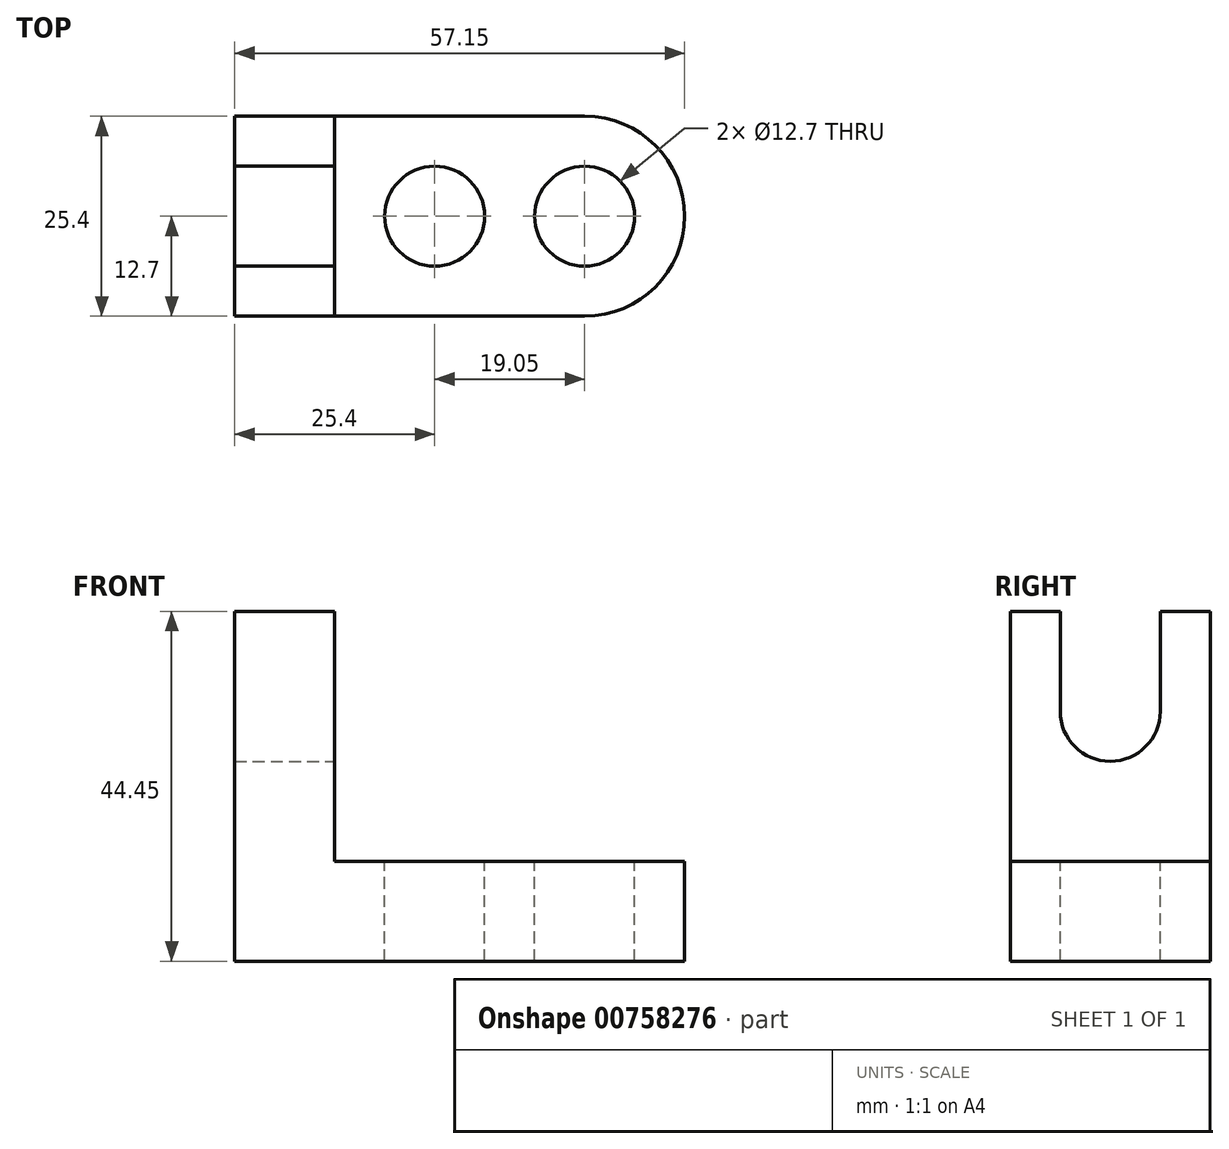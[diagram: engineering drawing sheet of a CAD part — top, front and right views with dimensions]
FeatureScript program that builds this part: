
annotation { "Feature Type Name" : "Feature", "Feature Type Description" : "" }
export const myFeature = defineFeature(function(context is Context, id is Id, definition is map)
    precondition{}
    {
        {
            var Q0;
            Q0=qCreatedBy(makeId("Front.planeOp"),FACE);
            var sketch = newSketch(context, id + "F0", { "sketchPlane" : qUnion([Q0])});
            skLineSegment(sketch, "E0", {"start": v(0, 0) * mm, "end": v(57.15, 0) * mm});
            skLineSegment(sketch, "E1", {"start": v(57.15, 0) * mm, "end": v(57.15, 44.45) * mm});
            skLineSegment(sketch, "E2", {"start": v(57.15, 44.45) * mm, "end": v(0, 44.45) * mm});
            skLineSegment(sketch, "E3", {"start": v(0, 44.45) * mm, "end": v(0, 0) * mm});
            skSolve(sketch);
        }
        {
            var Q0;
            Q0=makeQuery(id+"F0.imprint","IMPRINT",FACE,{"disambiguationData":[TD([[makeQuery(id+"F0.imprint","IMPRINT",EDGE,{"derivedFrom":sQuery(id+"F0.wireOp",EDGE,"E0")}),1.0]])]});
            extrude(context, id + "F1", {"entities" : qUnion([Q0]), "depth" : 25.4 * mm, "offsetDistance" : 25.4 * mm});
        }
        {
            var Q0;
            Q0=makeQuery(id+"F1.opExtrude","CAP_FACE",FACE,{"disambiguationData":[OSD([sQuery(id+"F0.wireOp",EDGE,"E0"),sQuery(id+"F0.wireOp",EDGE,"E1"),sQuery(id+"F0.wireOp",EDGE,"E2"),sQuery(id+"F0.wireOp",EDGE,"E3")])],"isStart":false});
            var sketch = newSketch(context, id + "F2", { "sketchPlane" : qUnion([Q0])});
            skLineSegment(sketch, "E4", {"start": v(12.7, 44.45) * mm, "end": v(12.7, 12.7) * mm});
            skLineSegment(sketch, "E5", {"start": v(12.7, 12.7) * mm, "end": v(57.15, 12.7) * mm});
            skSolve(sketch);
        }
        {
            var Q0;
            {var subQ0=sQuery(id+"F2.wireOp",EDGE,"E4");Q0=makeQuery(id+"F2.imprint","IMPRINT",FACE,{"disambiguationData":[TD([[makeQuery(id+"F2.imprint","IMPRINT",EDGE,{"derivedFrom":subQ0}),1.0]])]});}
            extrude(context, id + "F3", {"entities" : qUnion([Q0]), "operationType" : NewBodyOperationType.REMOVE, "oppositeDirection" : true, "depth" : 25.4 * mm, "offsetDistance" : 25.4 * mm});
        }
        {
            var Q0;
            Q0=makeQuery(id+"F3.boolean.opBoolean","COPY",FACE,{"derivedFrom":makeQuery(id+"F3.opExtrude","SWEPT_FACE",FACE,{"disambiguationData":[OSD([sQuery(id+"F2.wireOp",EDGE,"E5")])]})});
            var sketch = newSketch(context, id + "F4", { "sketchPlane" : qUnion([Q0])});
            skCircle(sketch, "E6", {"center": v(25.4, -12.7) * mm, "radius": 6.35 * mm});
            skCircle(sketch, "E7", {"center": v(44.45, -12.7) * mm, "radius": 6.35 * mm});
            skSolve(sketch);
        }
        {
            var Q0;
            Q0=makeQuery(id+"F4.imprint","IMPRINT",FACE,{"disambiguationData":[TD([[makeQuery(id+"F4.imprint","IMPRINT",EDGE,{"derivedFrom":sQuery(id+"F4.wireOp",EDGE,"E6")}),1.0]])]});
            var Q1;
            Q1=makeQuery(id+"F4.imprint","IMPRINT",FACE,{"disambiguationData":[TD([[makeQuery(id+"F4.imprint","IMPRINT",EDGE,{"derivedFrom":sQuery(id+"F4.wireOp",EDGE,"E7")}),1.0]])]});
            extrude(context, id + "F5", {"entities" : qUnion([Q0, Q1]), "operationType" : NewBodyOperationType.REMOVE, "oppositeDirection" : true, "depth" : 25.4 * mm, "offsetDistance" : 25.4 * mm});
        }
        {
            var Q0;
            Q0=makeQuery(id+"F3.boolean.opBoolean","COPY",FACE,{"derivedFrom":makeQuery(id+"F3.opExtrude","SWEPT_FACE",FACE,{"disambiguationData":[OSD([sQuery(id+"F2.wireOp",EDGE,"E5")])]})});
            var sketch = newSketch(context, id + "F6", { "sketchPlane" : qUnion([Q0])});
            skArc(sketch, "E8", {"start": v(44.45, -25.4) * mm, "mid": v(57.15, -12.7) * mm, "end": v(44.45, 0) * mm});
            skSolve(sketch);
        }
        {
            var Q0;
            {var subQ0=sQuery(id+"F6.wireOp",EDGE,"E8");var subQ1=sQuery(id+"F2.wireOp",EDGE,"E5");var subQ2=makeQuery(id+"F3.boolean.opBoolean","COPY",EDGE,{"derivedFrom":makeQuery(id+"F3.opExtrude","CAP_EDGE",EDGE,{"disambiguationData":[OSD([subQ1])],"isStart":false})});var subQ3=makeQuery(id+"F6.imprint","INTERSECT",VERTEX,{"derivedFrom":[subQ2,subQ0]});Q0=makeQuery(id+"F6.imprint","IMPRINT",FACE,{"disambiguationData":[TD([[makeQuery(id+"F6.imprint","IMPRINT",EDGE,{"disambiguationData":[TD([[subQ3,1.0]])],"derivedFrom":subQ0}),-1.0]])]});}
            var Q1;
            {var subQ0=sQuery(id+"F6.wireOp",EDGE,"E8");var subQ1=sQuery(id+"F2.wireOp",EDGE,"E5");var subQ2=makeQuery(id+"F3.boolean.opBoolean","COPY",EDGE,{"derivedFrom":makeQuery(id+"F3.opExtrude","CAP_EDGE",EDGE,{"disambiguationData":[OSD([subQ1])],"isStart":true})});var subQ3=makeQuery(id+"F6.imprint","INTERSECT",VERTEX,{"derivedFrom":[subQ2,subQ0]});Q1=makeQuery(id+"F6.imprint","IMPRINT",FACE,{"disambiguationData":[TD([[makeQuery(id+"F6.imprint","IMPRINT",EDGE,{"disambiguationData":[TD([[subQ3,-1.0]])],"derivedFrom":subQ0}),-1.0]])]});}
            extrude(context, id + "F7", {"entities" : qUnion([Q0, Q1]), "operationType" : NewBodyOperationType.REMOVE, "oppositeDirection" : true, "depth" : 25.4 * mm, "offsetDistance" : 25.4 * mm});
        }
        {
            var Q0;
            Q0=makeQuery(id+"F3.boolean.opBoolean","COPY",FACE,{"derivedFrom":makeQuery(id+"F3.opExtrude","SWEPT_FACE",FACE,{"disambiguationData":[OSD([sQuery(id+"F2.wireOp",EDGE,"E4")])]})});
            var sketch = newSketch(context, id + "F8", { "sketchPlane" : qUnion([Q0])});
            skCircle(sketch, "E9", {"center": v(-12.7, 31.75) * mm, "radius": 6.35 * mm});
            skLineSegment(sketch, "E10", {"start": v(-19.05, 31.75) * mm, "end": v(-19.05, 44.45) * mm});
            skLineSegment(sketch, "E11", {"start": v(-6.35, 31.75) * mm, "end": v(-6.35, 44.45) * mm});
            skArc(sketch, "E12", {"start": v(0, 31.75) * mm, "mid": v(-12.7, 44.45) * mm, "end": v(-25.4, 31.75) * mm});
            skPoint(sketch, "E12.endSnap0", {"position": v(-25.4, 28.57) * mm});
            skSolve(sketch);
        }
        {
            var Q0;
            {var subQ1=sQuery(id+"F2.wireOp",EDGE,"E4");var subQ4=sQuery(id+"F8.wireOp",EDGE,"E12");var subQ6=makeQuery(id+"F3.boolean.opBoolean","COPY",EDGE,{"derivedFrom":makeQuery(id+"F3.opExtrude","CAP_EDGE",EDGE,{"disambiguationData":[OSD([subQ1])],"isStart":true})});var subQ7=makeQuery(id+"F8.imprint","INTERSECT",VERTEX,{"derivedFrom":[subQ6,subQ4]});Q0=makeQuery(id+"F8.imprint","IMPRINT",FACE,{"disambiguationData":[TD([[makeQuery(id+"F8.imprint","IMPRINT",EDGE,{"disambiguationData":[TD([[subQ7,1.0]])],"derivedFrom":subQ4}),-1.0]])]});}
            var Q1;
            {var subQ1=sQuery(id+"F2.wireOp",EDGE,"E4");var subQ4=sQuery(id+"F8.wireOp",EDGE,"E12");var subQ6=makeQuery(id+"F3.boolean.opBoolean","COPY",EDGE,{"derivedFrom":makeQuery(id+"F3.opExtrude","CAP_EDGE",EDGE,{"disambiguationData":[OSD([subQ1])],"isStart":false})});var subQ7=makeQuery(id+"F8.imprint","INTERSECT",VERTEX,{"derivedFrom":[subQ6,subQ4]});Q1=makeQuery(id+"F8.imprint","IMPRINT",FACE,{"disambiguationData":[TD([[makeQuery(id+"F8.imprint","IMPRINT",EDGE,{"disambiguationData":[TD([[subQ7,-1.0]])],"derivedFrom":subQ4}),-1.0]])]});}
            var Q2;
            {var subQ0=sQuery(id+"F8.wireOp",EDGE,"E9");var subQ1=makeQuery(id+"F8.imprint","INTERSECT",VERTEX,{"derivedFrom":[subQ0,sQuery(id+"F8.wireOp",EDGE,"E10")]});Q2=makeQuery(id+"F8.imprint","IMPRINT",FACE,{"disambiguationData":[TD([[makeQuery(id+"F8.imprint","IMPRINT",EDGE,{"disambiguationData":[TD([[subQ1,1.0]])],"derivedFrom":subQ0}),1.0]])]});}
            var Q3;
            {var subQ1=sQuery(id+"F8.wireOp",EDGE,"E9");var subQ6=sQuery(id+"F8.wireOp",EDGE,"E10");var subQ7=makeQuery(id+"F8.imprint","INTERSECT",VERTEX,{"derivedFrom":[subQ1,subQ6]});Q3=makeQuery(id+"F8.imprint","IMPRINT",FACE,{"disambiguationData":[TD([[makeQuery(id+"F8.imprint","IMPRINT",EDGE,{"disambiguationData":[TD([[subQ7,1.0]])],"derivedFrom":subQ1}),-1.0]])]});}
            var Q4;
            {var subQ0=sQuery(id+"F8.wireOp",EDGE,"E10");var subQ3=sQuery(id+"F8.wireOp",EDGE,"E12");var subQ4=makeQuery(id+"F8.imprint","INTERSECT",VERTEX,{"derivedFrom":[subQ0,subQ3]});Q4=makeQuery(id+"F8.imprint","IMPRINT",FACE,{"disambiguationData":[TD([[makeQuery(id+"F8.imprint","IMPRINT",EDGE,{"disambiguationData":[TD([[subQ4,-1.0]])],"derivedFrom":subQ0}),-1.0]])]});}
            var Q5;
            {var subQ0=sQuery(id+"F8.wireOp",EDGE,"E11");var subQ3=sQuery(id+"F8.wireOp",EDGE,"E12");var subQ4=makeQuery(id+"F8.imprint","INTERSECT",VERTEX,{"derivedFrom":[subQ0,subQ3]});Q5=makeQuery(id+"F8.imprint","IMPRINT",FACE,{"disambiguationData":[TD([[makeQuery(id+"F8.imprint","IMPRINT",EDGE,{"disambiguationData":[TD([[subQ4,-1.0]])],"derivedFrom":subQ0}),1.0]])]});}
            extrude(context, id + "F9", {"entities" : qUnion([Q0, Q1, Q2, Q3, Q4, Q5]), "operationType" : NewBodyOperationType.REMOVE, "oppositeDirection" : true, "depth" : 25.4 * mm, "offsetDistance" : 25.4 * mm});
        }
    });
